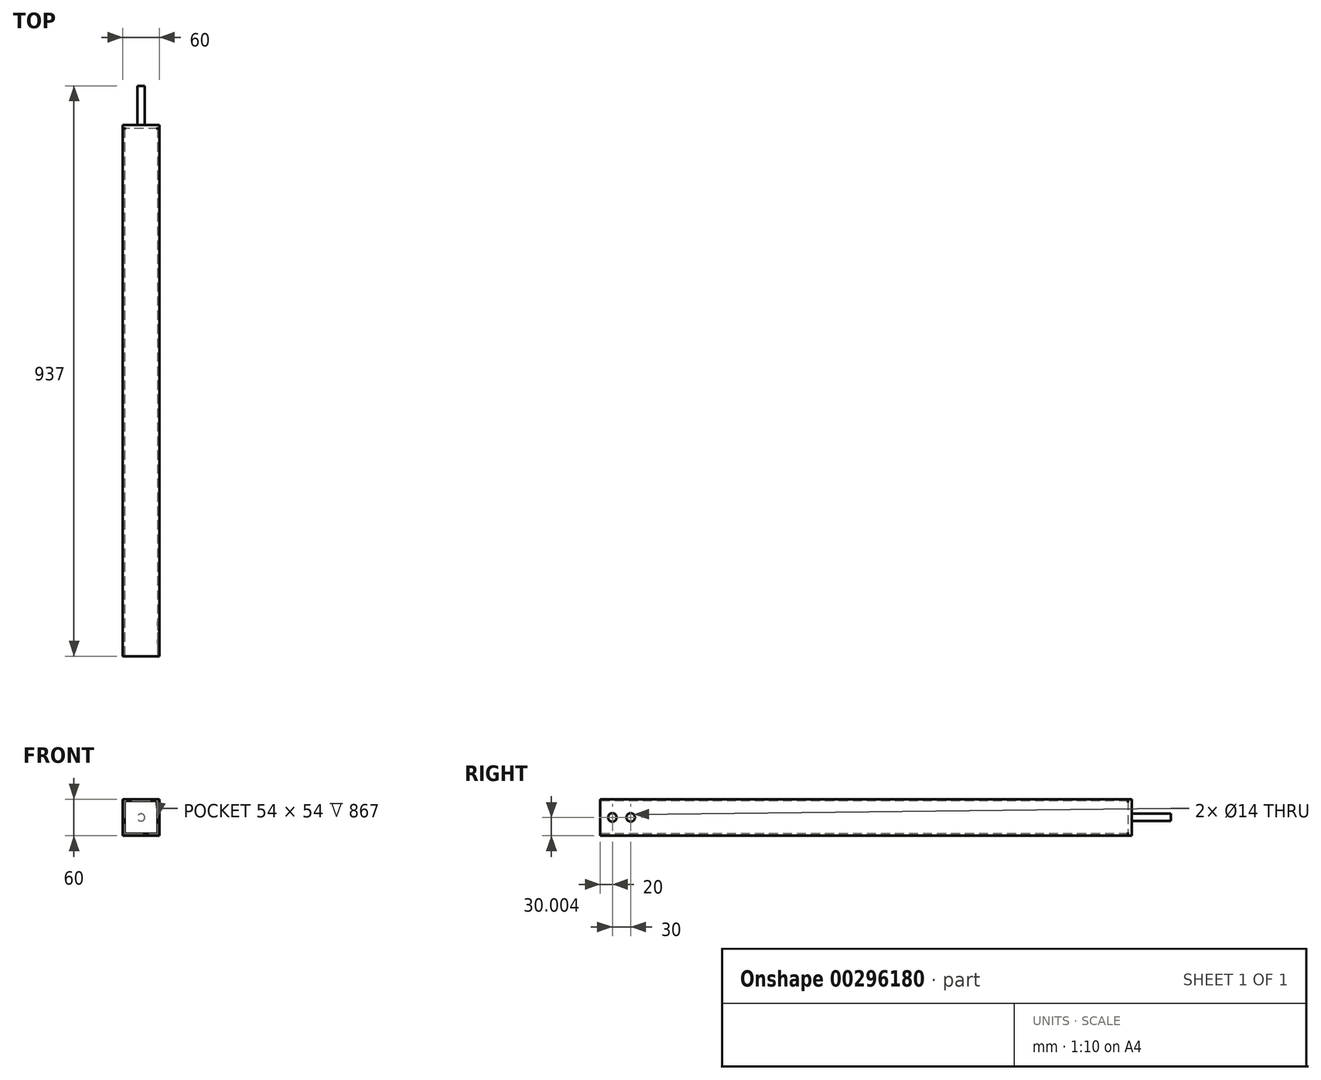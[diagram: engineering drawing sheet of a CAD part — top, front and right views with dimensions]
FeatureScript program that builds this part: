
annotation { "Feature Type Name" : "Feature", "Feature Type Description" : "" }
export const myFeature = defineFeature(function(context is Context, id is Id, definition is map)
    precondition{}
    {
        {
            var Q0;
            Q0=qCreatedBy(makeId("Front.planeOp"),FACE);
            var sketch = newSketch(context, id + "F0", { "sketchPlane" : qUnion([Q0])});
            skLineSegment(sketch, "E0.bottom", {"start": v(-33.99, -56) * mm, "end": v(-83.99, -56) * mm});
            skLineSegment(sketch, "E0.top", {"start": v(-33.99, -116) * mm, "end": v(-83.99, -116) * mm});
            skLineSegment(sketch, "E0.left", {"start": v(-28.99, -61) * mm, "end": v(-28.99, -111) * mm});
            skLineSegment(sketch, "E0.right", {"start": v(-88.99, -61) * mm, "end": v(-88.99, -111) * mm});
            skPoint(sketch, "E0.middle", {"position": v(-58.99, -86) * mm});
            skPoint(sketch, "E1.visualSharp", {"position": v(-88.99, -56) * mm});
            skArc(sketch, "E1.filletArc", {"start": v(-83.99, -56) * mm, "mid": v(-87.52, -57.46) * mm, "end": v(-88.99, -61) * mm});
            skPoint(sketch, "E2.visualSharp", {"position": v(-28.99, -56) * mm});
            skArc(sketch, "E2.filletArc", {"start": v(-28.99, -61) * mm, "mid": v(-30.45, -57.46) * mm, "end": v(-33.99, -56) * mm});
            skPoint(sketch, "E3.visualSharp", {"position": v(-28.99, -116) * mm});
            skArc(sketch, "E3.filletArc", {"start": v(-33.99, -116) * mm, "mid": v(-30.45, -114.53) * mm, "end": v(-28.99, -111) * mm});
            skPoint(sketch, "E4.visualSharp", {"position": v(-88.99, -116) * mm});
            skArc(sketch, "E4.filletArc", {"start": v(-88.99, -111) * mm, "mid": v(-87.52, -114.53) * mm, "end": v(-83.99, -116) * mm});
            skLineSegment(sketch, "E5.0", {"start": v(-31.99, -113) * mm, "end": v(-85.99, -113) * mm});
            skLineSegment(sketch, "E5.1", {"start": v(-31.99, -59) * mm, "end": v(-31.99, -113) * mm});
            skLineSegment(sketch, "E5.2", {"start": v(-31.99, -59) * mm, "end": v(-85.99, -59) * mm});
            skLineSegment(sketch, "E5.3", {"start": v(-85.99, -59) * mm, "end": v(-85.99, -113) * mm});
            skSolve(sketch);
        }
        {
            var Q0;
            Q0=makeQuery(id+"F0.imprint","IMPRINT",FACE,{"disambiguationData":[TD([[makeQuery(id+"F0.imprint","IMPRINT",EDGE,{"derivedFrom":sQuery(id+"F0.wireOp",EDGE,"WBqOBU3J-LVuc-RZdo-IQ9V-Ewm5Q1t9rkOa.bottom")}),1.0]])]});
            var Q1;
            Q1=makeQuery(id+"F0.imprint","IMPRINT",FACE,{"disambiguationData":[TD([[makeQuery(id+"F0.imprint","IMPRINT",EDGE,{"derivedFrom":sQuery(id+"F0.wireOp",EDGE,"99b7a4c1-c7c6-4472-a640-d268f497dcd0.bottom")}),1.0]])]});
            var Q2;
            Q2=makeQuery(id+"F0.imprint","IMPRINT",FACE,{"disambiguationData":[TD([[makeQuery(id+"F0.imprint","IMPRINT",EDGE,{"derivedFrom":sQuery(id+"F0.wireOp",EDGE,"E0.bottom")}),1.0]])]});
            extrude(context, id + "F1", {"entities" : qUnion([Q0, Q1, Q2]), "oppositeDirection" : true, "depth" : 867 * mm});
        }
        {
            var Q0;
            Q0=makeQuery(id+"F1.opExtrude","SWEPT_FACE",FACE,{"disambiguationData":[OSD([sQuery(id+"F0.wireOp",EDGE,"E0.left")])]});
            var sketch = newSketch(context, id + "F2", { "sketchPlane" : qUnion([Q0])});
            skLineSegment(sketch, "E6", {"start": v(0, -86) * mm, "end": v(867, -86) * mm, "construction": true});
            skCircle(sketch, "E7", {"center": v(20, -86) * mm, "radius": 7 * mm});
            skCircle(sketch, "E8", {"center": v(50, -86) * mm, "radius": 7 * mm});
            skSolve(sketch);
        }
        {
            var Q0;
            Q0=makeQuery(id+"F2.imprint","IMPRINT",FACE,{"disambiguationData":[TD([[makeQuery(id+"F2.imprint","IMPRINT",EDGE,{"derivedFrom":sQuery(id+"F2.wireOp",EDGE,"E7")}),1.0]])]});
            var Q1;
            Q1=makeQuery(id+"F2.imprint","IMPRINT",FACE,{"disambiguationData":[TD([[makeQuery(id+"F2.imprint","IMPRINT",EDGE,{"derivedFrom":sQuery(id+"F2.wireOp",EDGE,"E8")}),1.0]])]});
            var Q2;
            Q2=makeQuery(id+"F2.imprint","IMPRINT",FACE,{"disambiguationData":[TD([[makeQuery(id+"F2.imprint","IMPRINT",EDGE,{"derivedFrom":sQuery(id+"F2.wireOp",EDGE,"PXoqdurB-Hc8U-pkIU-v74U-M0RVBvyIfiNg")}),1.0]])]});
            var Q3;
            Q3=makeQuery(id+"F2.imprint","IMPRINT",FACE,{"disambiguationData":[TD([[makeQuery(id+"F2.imprint","IMPRINT",EDGE,{"derivedFrom":sQuery(id+"F2.wireOp",EDGE,"xU58mOWj-gC4y-5jYu-jP39-JdSxKQGVCWHp")}),1.0]])]});
            extrude(context, id + "F3", {"entities" : qUnion([Q0, Q1, Q2, Q3]), "operationType" : NewBodyOperationType.REMOVE, "endBound" : BoundingType.UP_TO_NEXT, "oppositeDirection" : true, "depth" : 25 * mm});
        }
        {
            var Q0;
            Q0=makeQuery(id+"F1.opExtrude","CAP_FACE",FACE,{"disambiguationData":[OSD([sQuery(id+"F0.wireOp",EDGE,"E0.bottom"),sQuery(id+"F0.wireOp",EDGE,"E0.top"),sQuery(id+"F0.wireOp",EDGE,"E0.left"),sQuery(id+"F0.wireOp",EDGE,"E0.right"),sQuery(id+"F0.wireOp",EDGE,"E1.filletArc"),sQuery(id+"F0.wireOp",EDGE,"E2.filletArc"),sQuery(id+"F0.wireOp",EDGE,"E3.filletArc"),sQuery(id+"F0.wireOp",EDGE,"E4.filletArc"),sQuery(id+"F0.wireOp",EDGE,"E5.0"),sQuery(id+"F0.wireOp",EDGE,"E5.1"),sQuery(id+"F0.wireOp",EDGE,"E5.2"),sQuery(id+"F0.wireOp",EDGE,"E5.3")])],"isStart":false});
            var sketch = newSketch(context, id + "F4", { "sketchPlane" : qUnion([Q0])});
            skLineSegment(sketch, "E9.bottom", {"start": v(88.99, -56) * mm, "end": v(28.99, -56) * mm});
            skLineSegment(sketch, "E9.top", {"start": v(88.99, -116) * mm, "end": v(28.99, -116) * mm});
            skLineSegment(sketch, "E9.left", {"start": v(88.99, -56) * mm, "end": v(88.99, -116) * mm});
            skLineSegment(sketch, "E9.right", {"start": v(28.99, -56) * mm, "end": v(28.99, -116) * mm});
            skCircle(sketch, "E10", {"center": v(58.99, -86) * mm, "radius": 6 * mm});
            skSolve(sketch);
        }
        {
            var Q0;
            Q0 = qSketchRegion(id + "F4", true);
            extrude(context, id + "F5", {"entities" : qUnion([Q0]), "operationType" : NewBodyOperationType.ADD, "depth" : 6 * mm});
        }
        {
            var Q0;
            Q0=makeQuery(id+"F5.opExtrude","CAP_FACE",FACE,{"disambiguationData":[OSD([sQuery(id+"F4.wireOp",EDGE,"E9.bottom"),sQuery(id+"F4.wireOp",EDGE,"E9.top"),sQuery(id+"F4.wireOp",EDGE,"E9.left"),sQuery(id+"F4.wireOp",EDGE,"E9.right"),sQuery(id+"F4.wireOp",EDGE,"E10")])],"isStart":false});
            cPlane(context, id + "F6", {"entities" : qUnion([Q0]), "cplaneType" : CPlaneType.OFFSET, "offset" : 6 * mm, "oppositeDirection" : true, "width" : 150 * mm, "height" : 150 * mm});
        }
        {
            var Q0;
            Q0=qCreatedBy(id+"F6.planeOp",FACE);
            var sketch = newSketch(context, id + "F7", { "sketchPlane" : qUnion([Q0])});
            skCircle(sketch, "E11", {"center": v(58.99, -86) * mm, "radius": 6 * mm});
            skSolve(sketch);
        }
        {
            var Q0;
            Q0 = qSketchRegion(id + "F7", true);
            extrude(context, id + "F8", {"entities" : qUnion([Q0]), "operationType" : NewBodyOperationType.ADD, "depth" : 70 * mm});
        }
    });
